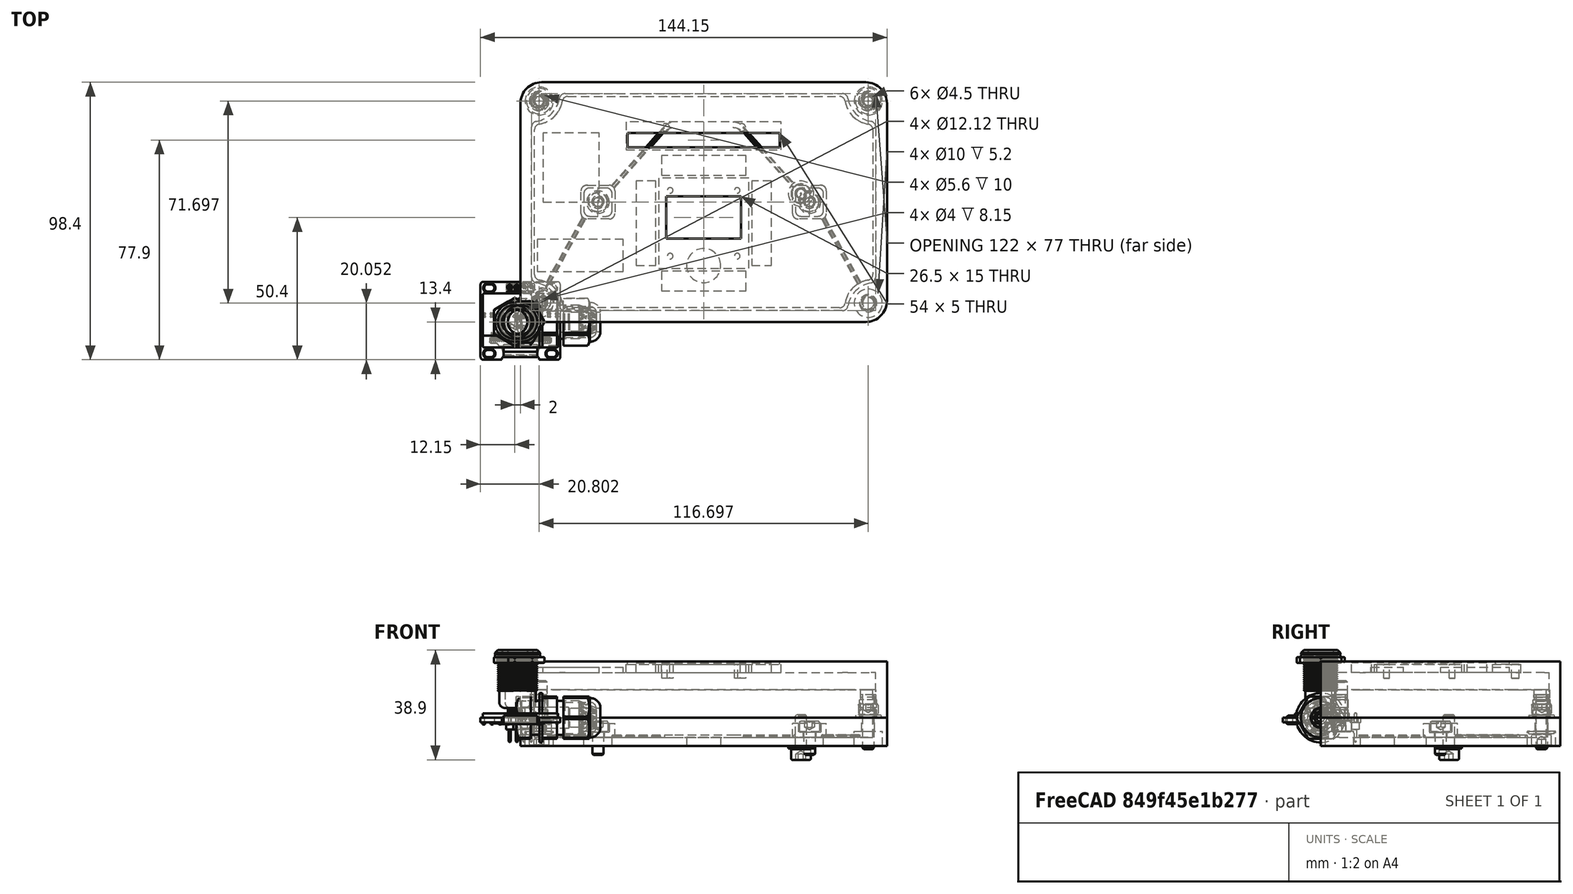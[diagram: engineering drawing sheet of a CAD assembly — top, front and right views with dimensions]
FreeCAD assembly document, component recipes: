
FREECAD ASSEMBLY — COMPONENT RECIPES ("FirstDraft_backup")

This assembly document has 6 components, labeled P0..P5 below (a component is one placed body or linked part). 2 of them carry a construction recipe — the FreeCAD feature program that regenerates the part from scratch, quoted from this document or its linked companion documents; the rest are supplied as boundary geometry only. No exploded tour is included for this assembly.
COMPONENT P0 — geometry summary ("Assembly"; no construction recipe available for this part):
  bounding box: 130.0 x 85.0 x 34.9 mm
  tessellated surface: 4,214 triangles
  volume: 3711431108486188694012094726733340963305844583327814948994821597056413378475866344786778061308690432 mm^3 (962395765290224016531339386291263704260556717746490642713404556607119533521990315734207654002688% of its bounding box)
COMPONENT P1 — recipe-attached ("Base", modeled in this document).
Construction recipe (the document's own serialized feature program — sketch geometry with constraints, then the solid features built on it; lengths are millimeters unless a unit is written):

FEATURE [PartDesign::ShapeBinder] ShapeBinder
  Support = -> [Pocket]
  TraceSupport = true
FEATURE [Sketcher::SketchObject] Sketch010
  ExternalGeometry = -> [ShapeBinder]
  FullyConstrained = true
  MapMode = 5
  Placement = pos=(0,0,0) rot=(1,0,0;3.14159rad)
  Support = -> [ShapeBinder]
  sketch-geometry (23):
    g0: GeomPoint X=5 Y=-5 Z=0
    g1: GeomPoint X=125 Y=-80 Z=0
    g2: GeomPoint X=65 Y=-42.5 Z=0
    g3: ArcOfCircle CenterX=5 CenterY=-80 CenterZ=0 NormalX=0 NormalY=0 NormalZ=1 AngleXU=0 Radius=10 StartAngle=0.167448 EndAngle=1.40335
    g4: ArcOfCircle CenterX=7 CenterY=-68.1678 CenterZ=0 NormalX=0 NormalY=0 NormalZ=1 AngleXU=0 Radius=2 StartAngle=3.14159 EndAngle=4.54494
    g5: ArcOfCircle CenterX=5 CenterY=-5 CenterZ=0 NormalX=0 NormalY=0 NormalZ=1 AngleXU=0 Radius=10 StartAngle=4.87984 EndAngle=6.11574
    g6: ArcOfCircle CenterX=125 CenterY=-5 CenterZ=0 NormalX=0 NormalY=0 NormalZ=1 AngleXU=0 Radius=10 StartAngle=3.30904 EndAngle=4.54494
    g7: ArcOfCircle CenterX=125 CenterY=-80 CenterZ=0 NormalX=0 NormalY=0 NormalZ=1 AngleXU=0 Radius=10 StartAngle=1.73824 EndAngle=2.97414
    g8: LineSegment StartX=5 StartY=-80 StartZ=0 EndX=125 EndY=-80 EndZ=0
    g9: LineSegment StartX=125 StartY=-80 StartZ=0 EndX=125 EndY=-5 EndZ=0
    g10: LineSegment StartX=5 StartY=-5 StartZ=0 EndX=5 EndY=-80 EndZ=0
    g11: ArcOfCircle CenterX=7 CenterY=-16.8322 CenterZ=0 NormalX=0 NormalY=0 NormalZ=1 AngleXU=0 Radius=2 StartAngle=1.73824 EndAngle=3.14159
    g12: ArcOfCircle CenterX=123 CenterY=-16.8322 CenterZ=0 NormalX=0 NormalY=0 NormalZ=1 AngleXU=0 Radius=2 StartAngle=9e-16 EndAngle=1.40335
    g13: ArcOfCircle CenterX=16.8322 CenterY=-7 CenterZ=0 NormalX=0 NormalY=0 NormalZ=1 AngleXU=0 Radius=2 StartAngle=1.5708 EndAngle=2.97414
    g14: ArcOfCircle CenterX=113.168 CenterY=-7 CenterZ=0 NormalX=0 NormalY=0 NormalZ=1 AngleXU=0 Radius=2 StartAngle=0.167448 EndAngle=1.5708
    g15: ArcOfCircle CenterX=123 CenterY=-68.1678 CenterZ=0 NormalX=0 NormalY=0 NormalZ=1 AngleXU=0 Radius=2 StartAngle=4.87984 EndAngle=6.28319
    g16: ArcOfCircle CenterX=113.168 CenterY=-78 CenterZ=0 NormalX=0 NormalY=0 NormalZ=1 AngleXU=0 Radius=2 StartAngle=4.71239 EndAngle=6.11574
    g17: ArcOfCircle CenterX=16.8322 CenterY=-78 CenterZ=0 NormalX=0 NormalY=0 NormalZ=1 AngleXU=0 Radius=2 StartAngle=3.30904 EndAngle=4.71239
    g18: LineSegment StartX=5 StartY=-5 StartZ=0 EndX=125 EndY=-5 EndZ=0
    g19: LineSegment StartX=5 StartY=-16.8322 StartZ=0 EndX=5 EndY=-68.1678 EndZ=0
    g20: LineSegment StartX=125 StartY=-68.1678 StartZ=0 EndX=125 EndY=-16.8322 EndZ=0
    g21: LineSegment StartX=113.168 StartY=-5 StartZ=0 EndX=16.8322 EndY=-5 EndZ=0
    g22: LineSegment StartX=16.8322 StartY=-80 StartZ=0 EndX=113.168 EndY=-80 EndZ=0
  constraints (54):
    c: Tangent(g3,g4) = 1.5708
    c: Coincident(g7,g1)
    c: Coincident(g8,g9)
    c: Coincident(g10,g8)
    c: Horizontal(g8)
    c: Vertical(g9)
    c: Vertical(g10)
    c: Coincident(g8,g3)
    c: Coincident(g9,g6)
    c: Coincident(g0,g5)
    c: Symmetric(g3,g6,g2)
    c: Tangent(g5,g11) = 1.5708
    c: Tangent(g6,g12) = 1.5708
    c: Tangent(g5,g13) = 1.5708
    c: Tangent(g6,g14) = 1.5708
    c: Tangent(g7,g15) = 1.5708
    c: Tangent(g7,g16) = 1.5708
    c: Equal(g3,g5)
    c: Equal(g5,g6)
    c: Equal(g6,g7)
    c: Radius(g3) = 10
    c: Equal(g4,g13)
    c: Equal(g13,g11)
    c: Equal(g11,g14)
    c: Equal(g12,g15)
    c: Tangent(g16,g8) = -1.5708
    c: Tangent(g4,g10) = -1.5708
    c: Coincident(g8,g7)
    c: Tangent(g17,g8) = -1.5708
    c: Tangent(g17,g3) = 1.5708
    c: Radius(g17) = 2
    c: Tangent(g12,g9) = -1.5708
    c: Tangent(g15,g9) = -1.5708
    c: Tangent(g11,g10) = -1.5708
    c: Coincident(g18,g5)
    c: Horizontal(g18)
    c: Coincident(g18,g6)
    c: Coincident(g10,g5)
    c: Tangent(g13,g18) = 1.5708
    c: Tangent(g14,g18) = 1.5708
    c: Equal(g11,g12)
    c: Equal(g14,g17)
    c: Equal(g17,g16)
    c: Symmetric(g-3,g-5,g2)
    c: Coincident(g19,g11)
    c: Coincident(g19,g4)
    c: Coincident(g20,g15)
    c: Coincident(g20,g12)
    c: Coincident(g21,g14)
    c: Coincident(g21,g13)
    c: DistanceY(g5,g-4) = 1
    c: DistanceX(g-5,g11) = 1
    c: Coincident(g22,g17)
    c: Coincident(g22,g16)
FEATURE [Sketcher::SketchObject] Sketch011
  ExternalGeometry = -> [ShapeBinder]
  FullyConstrained = true
  MapMode = 5
  Placement = pos=(0,0,0) rot=(1,0,0;3.14159rad)
  Support = -> [ShapeBinder]
  sketch-geometry (12):
    g0: LineSegment StartX=7.5 StartY=0 StartZ=0 EndX=122.5 EndY=0 EndZ=0
    g1: LineSegment StartX=130 StartY=-7.5 StartZ=0 EndX=130 EndY=-77.5 EndZ=0
    g2: LineSegment StartX=122.5 StartY=-85 StartZ=0 EndX=7.5 EndY=-85 EndZ=0
    g3: LineSegment StartX=0 StartY=-77.5 StartZ=0 EndX=0 EndY=-7.5 EndZ=0
    g4: ArcOfCircle CenterX=7.5 CenterY=-7.5 CenterZ=0 NormalX=0 NormalY=0 NormalZ=1 AngleXU=0 Radius=7.5 StartAngle=1.5708 EndAngle=3.14159
    g5: GeomPoint X=0 Y=0 Z=0
    g6: ArcOfCircle CenterX=122.5 CenterY=-7.5 CenterZ=0 NormalX=0 NormalY=0 NormalZ=1 AngleXU=0 Radius=7.5 StartAngle=0 EndAngle=1.5708
    g7: GeomPoint X=130 Y=0 Z=0
    g8: ArcOfCircle CenterX=122.5 CenterY=-77.5 CenterZ=0 NormalX=0 NormalY=0 NormalZ=1 AngleXU=0 Radius=7.5 StartAngle=4.71239 EndAngle=6.28319
    g9: GeomPoint X=130 Y=-85 Z=0
    g10: ArcOfCircle CenterX=7.5 CenterY=-77.5 CenterZ=0 NormalX=0 NormalY=0 NormalZ=1 AngleXU=0 Radius=7.5 StartAngle=3.14159 EndAngle=4.71239
    g11: GeomPoint X=0 Y=-85 Z=0
  constraints (23):
    c: Horizontal(g0)
    c: Vertical(g1)
    c: Vertical(g3)
    c: Coincident(g5,g-1)
    c: PointOnObject(g5,g3)
    c: Tangent(g0,g4) = 1.5708
    c: Tangent(g3,g4) = 1.5708
    c: PointOnObject(g7,g1)
    c: PointOnObject(g7,g0)
    c: Tangent(g1,g6) = 1.5708
    c: Tangent(g0,g6) = 1.5708
    c: PointOnObject(g9,g1)
    c: PointOnObject(g9,g2)
    c: Tangent(g1,g8) = 1.5708
    c: Tangent(g2,g8) = 1.5708
    c: PointOnObject(g11,g2)
    c: PointOnObject(g11,g3)
    c: Tangent(g2,g10) = 1.5708
    c: Tangent(g3,g10) = 1.5708
    c: Coincident(g2,g-4)
    c: Coincident(g2,g-4)
    c: Coincident(g-3,g1)
    c: Coincident(g0,g-5)
FEATURE [PartDesign::Pad] Pad003
  Direction = (0,0,-1)
  Length = 10
  Length2 = 10
  Profile = -> Sketch011
  ReferenceAxis = -> Sketch011 [N_Axis]
  Type = 0
FEATURE [PartDesign::Pocket] Pocket005
  BaseFeature = -> Pad003
  Direction = (0,0,1)
  Length = 7
  Length2 = 5
  Profile = -> Sketch010
  ReferenceAxis = -> Sketch010 [N_Axis]
  Reversed = true
  Type = 0
FEATURE [Sketcher::SketchObject] Sketch012
  ExternalGeometry = -> [ShapeBinder]
  FullyConstrained = true
  MapMode = 5
  Placement = pos=(0,0,-10) rot=(1,0,0;3.14159rad)
  Support = -> [Pocket005]
  sketch-geometry (4):
    g0: Circle CenterX=6.65146 CenterY=-6.65148 CenterZ=0 NormalX=0 NormalY=0 NormalZ=1 AngleXU=0 Radius=2.8
    g1: Circle CenterX=123.349 CenterY=-6.65148 CenterZ=0 NormalX=0 NormalY=0 NormalZ=1 AngleXU=0 Radius=2.8
    g2: Circle CenterX=123.349 CenterY=-78.3485 CenterZ=0 NormalX=0 NormalY=0 NormalZ=1 AngleXU=0 Radius=2.8
    g3: Circle CenterX=6.65146 CenterY=-78.3485 CenterZ=0 NormalX=0 NormalY=0 NormalZ=1 AngleXU=0 Radius=2.8
  constraints (8):
    c: Coincident(g1,g-4)
    c: Coincident(g2,g-5)
    c: Coincident(g3,g-6)
    c: Coincident(g0,g-3)
    c: Equal(g0,g-3)
    c: Equal(g0,g1)
    c: Equal(g1,g2)
    c: Equal(g2,g3)
FEATURE [PartDesign::Hole] Hole
  BaseFeature = -> Pocket005
  CustomThreadClearance = 0
  Depth = 314.401
  DepthType = 1
  Diameter = 4.5
  DrillForDepth = false
  DrillPoint = 1
  DrillPointAngle = 118
  HoleCutCountersinkAngle = 90
  HoleCutCustomValues = false
  HoleCutDepth = 5.2
  HoleCutDiameter = 10
  HoleCutType = 12
  ModelThread = false
  Profile = -> Sketch012
  Tapered = false
  TaperedAngle = 90
  ThreadClass = 0
  ThreadDepth = 314.401
  ThreadDepthType = 0
  ThreadDirection = 0
  ThreadFit = 0
  ThreadSize = 11
  ThreadType = 1
  Threaded = false
  UseCustomThreadClearance = false
FEATURE [Sketcher::SketchObject] Sketch013
  ExternalGeometry = -> [ShapeBinder]
  FullyConstrained = true
  MapMode = 5
  Placement = pos=(0,0,0) rot=(1,0,0;3.14159rad)
  Support = -> [ShapeBinder]
  sketch-geometry (46):
    g0: GeomPoint X=5 Y=-5 Z=0
    g1: GeomPoint X=125 Y=-80 Z=0
    g2: GeomPoint X=65 Y=-42.5 Z=0
    g3: ArcOfCircle CenterX=5 CenterY=-80 CenterZ=0 NormalX=0 NormalY=0 NormalZ=1 AngleXU=0 Radius=10 StartAngle=0.167448 EndAngle=1.40335
    g4: ArcOfCircle CenterX=7 CenterY=-68.1678 CenterZ=0 NormalX=0 NormalY=0 NormalZ=1 AngleXU=0 Radius=2 StartAngle=3.14159 EndAngle=4.54494
    g5: ArcOfCircle CenterX=5 CenterY=-5 CenterZ=0 NormalX=0 NormalY=0 NormalZ=1 AngleXU=0 Radius=10 StartAngle=4.87984 EndAngle=6.11574
    g6: ArcOfCircle CenterX=125 CenterY=-5 CenterZ=0 NormalX=0 NormalY=0 NormalZ=1 AngleXU=0 Radius=10 StartAngle=3.30904 EndAngle=4.54494
    g7: ArcOfCircle CenterX=125 CenterY=-80 CenterZ=0 NormalX=0 NormalY=0 NormalZ=1 AngleXU=0 Radius=10 StartAngle=1.73824 EndAngle=2.97414
    g8: LineSegment StartX=5 StartY=-80 StartZ=0 EndX=125 EndY=-80 EndZ=0
    g9: LineSegment StartX=125 StartY=-80 StartZ=0 EndX=125 EndY=-5 EndZ=0
    g10: LineSegment StartX=5 StartY=-5 StartZ=0 EndX=5 EndY=-80 EndZ=0
    g11: ArcOfCircle CenterX=7 CenterY=-16.8322 CenterZ=0 NormalX=0 NormalY=0 NormalZ=1 AngleXU=0 Radius=2 StartAngle=1.73824 EndAngle=3.14159
    g12: ArcOfCircle CenterX=123 CenterY=-16.8322 CenterZ=0 NormalX=0 NormalY=0 NormalZ=1 AngleXU=0 Radius=2 StartAngle=-9e-16 EndAngle=1.40335
    g13: ArcOfCircle CenterX=16.8322 CenterY=-7 CenterZ=0 NormalX=0 NormalY=0 NormalZ=1 AngleXU=0 Radius=2 StartAngle=1.5708 EndAngle=2.97414
    g14: ArcOfCircle CenterX=113.168 CenterY=-7 CenterZ=0 NormalX=0 NormalY=0 NormalZ=1 AngleXU=0 Radius=2 StartAngle=0.167448 EndAngle=1.5708
    g15: ArcOfCircle CenterX=123 CenterY=-68.1678 CenterZ=0 NormalX=0 NormalY=0 NormalZ=1 AngleXU=0 Radius=2 StartAngle=4.87984 EndAngle=6.28319
    g16: ArcOfCircle CenterX=113.168 CenterY=-78 CenterZ=0 NormalX=0 NormalY=0 NormalZ=1 AngleXU=0 Radius=2 StartAngle=4.71239 EndAngle=6.11574
    g17: ArcOfCircle CenterX=16.8322 CenterY=-78 CenterZ=0 NormalX=0 NormalY=0 NormalZ=1 AngleXU=0 Radius=2 StartAngle=3.30904 EndAngle=4.71239
    g18: LineSegment StartX=5 StartY=-5 StartZ=0 EndX=125 EndY=-5 EndZ=0
    g19: LineSegment StartX=5 StartY=-16.8322 StartZ=0 EndX=5 EndY=-68.1678 EndZ=0
    g20: LineSegment StartX=125 StartY=-68.1678 StartZ=0 EndX=125 EndY=-16.8322 EndZ=0
    g21: LineSegment StartX=113.168 StartY=-5 StartZ=0 EndX=16.8322 EndY=-5 EndZ=0
    g22: LineSegment StartX=16.8322 StartY=-80 StartZ=0 EndX=113.168 EndY=-80 EndZ=0
    g23: GeomPoint X=4 Y=-4 Z=0
    g24: GeomPoint X=126 Y=-81 Z=0
    g25: GeomPoint X=65 Y=-42.5 Z=0
    g26: ArcOfCircle CenterX=4 CenterY=-81 CenterZ=0 NormalX=0 NormalY=0 NormalZ=1 AngleXU=0 Radius=10 StartAngle=0.167448 EndAngle=1.40335
    g27: ArcOfCircle CenterX=6 CenterY=-69.1678 CenterZ=0 NormalX=0 NormalY=0 NormalZ=1 AngleXU=0 Radius=2 StartAngle=3.14159 EndAngle=4.54494
    g28: ArcOfCircle CenterX=4 CenterY=-4 CenterZ=0 NormalX=0 NormalY=0 NormalZ=1 AngleXU=0 Radius=10 StartAngle=4.87984 EndAngle=6.11574
    g29: ArcOfCircle CenterX=126 CenterY=-4 CenterZ=0 NormalX=0 NormalY=0 NormalZ=1 AngleXU=0 Radius=10 StartAngle=3.30904 EndAngle=4.54494
    g30: ArcOfCircle CenterX=126 CenterY=-81 CenterZ=0 NormalX=0 NormalY=0 NormalZ=1 AngleXU=0 Radius=10 StartAngle=1.73824 EndAngle=2.97414
    g31: LineSegment StartX=4 StartY=-81 StartZ=0 EndX=126 EndY=-81 EndZ=0
    g32: LineSegment StartX=126 StartY=-81 StartZ=0 EndX=126 EndY=-4 EndZ=0
    g33: LineSegment StartX=4 StartY=-4 StartZ=0 EndX=4 EndY=-81 EndZ=0
    g34: ArcOfCircle CenterX=6 CenterY=-15.8322 CenterZ=0 NormalX=0 NormalY=0 NormalZ=1 AngleXU=0 Radius=2 StartAngle=1.73824 EndAngle=3.14159
    g35: ArcOfCircle CenterX=124 CenterY=-15.8322 CenterZ=0 NormalX=0 NormalY=0 NormalZ=1 AngleXU=0 Radius=2 StartAngle=3e-16 EndAngle=1.40335
    g36: ArcOfCircle CenterX=15.8322 CenterY=-6 CenterZ=0 NormalX=0 NormalY=0 NormalZ=1 AngleXU=0 Radius=2 StartAngle=1.5708 EndAngle=2.97414
    g37: ArcOfCircle CenterX=114.168 CenterY=-6 CenterZ=0 NormalX=0 NormalY=0 NormalZ=1 AngleXU=0 Radius=2 StartAngle=0.167448 EndAngle=1.5708
    g38: ArcOfCircle CenterX=124 CenterY=-69.1678 CenterZ=0 NormalX=0 NormalY=0 NormalZ=1 AngleXU=0 Radius=2 StartAngle=4.87984 EndAngle=6.28319
    g39: ArcOfCircle CenterX=114.168 CenterY=-79 CenterZ=0 NormalX=0 NormalY=0 NormalZ=1 AngleXU=0 Radius=2 StartAngle=4.71239 EndAngle=6.11574
    g40: ArcOfCircle CenterX=15.8322 CenterY=-79 CenterZ=0 NormalX=0 NormalY=0 NormalZ=1 AngleXU=0 Radius=2 StartAngle=3.30904 EndAngle=4.71239
    g41: LineSegment StartX=4 StartY=-4 StartZ=0 EndX=126 EndY=-4 EndZ=0
    g42: LineSegment StartX=4 StartY=-15.8322 StartZ=0 EndX=4 EndY=-69.1678 EndZ=0
    g43: LineSegment StartX=126 StartY=-69.1678 StartZ=0 EndX=126 EndY=-15.8322 EndZ=0
    g44: LineSegment StartX=114.168 StartY=-4 StartZ=0 EndX=15.8322 EndY=-4 EndZ=0
    g45: LineSegment StartX=15.8322 StartY=-81 StartZ=0 EndX=114.168 EndY=-81 EndZ=0
  constraints (107):
    c: Tangent(g3,g4) = 1.5708
    c: Coincident(g7,g1)
    c: Coincident(g8,g9)
    c: Coincident(g10,g8)
    c: Horizontal(g8)
    c: Vertical(g9)
    c: Vertical(g10)
    c: Coincident(g8,g3)
    c: Coincident(g9,g6)
    c: Coincident(g0,g5)
    c: Symmetric(g3,g6,g2)
    c: Tangent(g5,g11) = 1.5708
    c: Tangent(g6,g12) = 1.5708
    c: Tangent(g5,g13) = 1.5708
    c: Tangent(g6,g14) = 1.5708
    c: Tangent(g7,g15) = 1.5708
    c: Tangent(g7,g16) = 1.5708
    c: Equal(g3,g5)
    c: Equal(g5,g6)
    c: Equal(g6,g7)
    c: Radius(g3) = 10
    c: Equal(g4,g13)
    c: Equal(g13,g11)
    c: Equal(g11,g14)
    c: Equal(g12,g15)
    c: Tangent(g16,g8) = -1.5708
    c: Tangent(g4,g10) = -1.5708
    c: Coincident(g8,g7)
    c: Tangent(g17,g8) = -1.5708
    c: Tangent(g17,g3) = 1.5708
    c: Radius(g17) = 2
    c: Tangent(g12,g9) = -1.5708
    c: Tangent(g15,g9) = -1.5708
    c: Tangent(g11,g10) = -1.5708
    c: Coincident(g18,g5)
    c: Horizontal(g18)
    c: Coincident(g18,g6)
    c: Coincident(g10,g5)
    c: Tangent(g13,g18) = 1.5708
    c: Tangent(g14,g18) = 1.5708
    c: Equal(g11,g12)
    c: Equal(g14,g17)
    c: Equal(g17,g16)
    c: Coincident(g19,g11)
    c: Coincident(g19,g4)
    c: Coincident(g20,g15)
    c: Coincident(g20,g12)
    c: Coincident(g21,g14)
    c: Coincident(g21,g13)
    c: Coincident(g22,g17)
    c: Coincident(g22,g16)
    c: Tangent(g26,g27) = 1.5708
    c: Coincident(g30,g24)
    c: Coincident(g31,g32)
    c: Coincident(g33,g31)
    c: Horizontal(g31)
    c: Vertical(g32)
    c: Vertical(g33)
    c: Coincident(g31,g26)
    c: Coincident(g32,g29)
    c: Coincident(g23,g28)
    c: Symmetric(g26,g29,g25)
    c: Tangent(g28,g34) = 1.5708
    c: Tangent(g29,g35) = 1.5708
    c: Tangent(g28,g36) = 1.5708
    c: Tangent(g29,g37) = 1.5708
    c: Tangent(g30,g38) = 1.5708
    c: Tangent(g30,g39) = 1.5708
    c: Equal(g26,g28)
    c: Equal(g28,g29)
    c: Equal(g29,g30)
    c: Radius(g26) = 10
    c: Equal(g27,g36)
    c: Equal(g36,g34)
    c: Equal(g34,g37)
    c: Equal(g35,g38)
    c: Tangent(g39,g31) = -1.5708
    c: Tangent(g27,g33) = -1.5708
    c: Coincident(g31,g30)
    c: Tangent(g40,g31) = -1.5708
    c: Tangent(g40,g26) = 1.5708
    c: Radius(g40) = 2
    c: Tangent(g35,g32) = -1.5708
    c: Tangent(g38,g32) = -1.5708
    c: Tangent(g34,g33) = -1.5708
    c: Coincident(g41,g28)
    c: Horizontal(g41)
    c: Coincident(g41,g29)
    c: Coincident(g33,g28)
    c: Tangent(g36,g41) = 1.5708
    c: Tangent(g37,g41) = 1.5708
    c: Equal(g34,g35)
    c: Equal(g37,g40)
    c: Equal(g40,g39)
    c: Coincident(g42,g34)
    c: Coincident(g42,g27)
    c: Coincident(g43,g38)
    c: Coincident(g43,g35)
    c: Coincident(g44,g37)
    c: Coincident(g44,g36)
    c: Coincident(g45,g40)
    c: Coincident(g45,g39)
    c: Symmetric(g28,g30,g2)
    c: Coincident(g34,g-3)
    c: Coincident(g38,g-4)
    c: DistanceX(g27,g4) = 1
    c: DistanceY(g40,g17) = 1
FEATURE [PartDesign::Pad] Pad004
  BaseFeature = -> Hole
  Direction = (0,0,-1)
  Length = 10
  Length2 = 10
  Profile = -> Sketch013
  ReferenceAxis = -> Sketch013 [N_Axis]
  Reversed = true
  Type = 0
FEATURE [PartDesign::CoordinateSystem] LCS_1
  AttacherType = Attacher::AttachEngine3D
  MapMode = 5
  Support = -> [Pad004]
FEATURE [PartDesign::Line] HoleAxis_1
  AttacherType = Attacher::AttachEngineLine
  Length = 4.79083
  MapMode = 19
  Placement = pos=(123.349,6.65148,-4.8) rot=(0,1,0;3.14159rad)
  ResizeMode = 1
  Support = -> [Pad004]
FEATURE [PartDesign::Line] HoleAxis_2
  AttacherType = Attacher::AttachEngineLine
  Length = 4.79083
  MapMode = 19
  Placement = pos=(123.349,78.3485,-4.8) rot=(0,1,0;3.14159rad)
  ResizeMode = 1
  Support = -> [Pad004]
FEATURE [PartDesign::Line] HoleAxis_3
  AttacherType = Attacher::AttachEngineLine
  Length = 4.79083
  MapMode = 19
  Placement = pos=(6.65146,78.3485,-4.8) rot=(0,1,0;3.14159rad)
  ResizeMode = 1
  Support = -> [Pad004]
FEATURE [PartDesign::Line] HoleAxis_4
  AttacherType = Attacher::AttachEngineLine
  Length = 4.79083
  MapMode = 19
  Placement = pos=(6.65146,6.65148,-4.8) rot=(0,1,0;3.14159rad)
  ResizeMode = 1
  Support = -> [Pad004]
FEATURE [Sketcher::SketchObject] Sketch014
  ExternalGeometry = -> [Pad004]
  FullyConstrained = true
  MapMode = 5
  Placement = pos=(0,0,-7) rot=(0,0,1;0rad)
  Support = -> [Pad004]
  sketch-geometry (3):
    g0: Circle CenterX=65 CenterY=20 CenterZ=0 NormalX=0 NormalY=0 NormalZ=1 AngleXU=0 Radius=6
    g1: GeomPoint X=65 Y=0 Z=0
    g2: LineSegment StartX=65 StartY=0 StartZ=0 EndX=65 EndY=20 EndZ=0
  constraints (6):
    c: Diameter(g0) = 12
    c: Symmetric(g-3,g-3,g1)
    c: Coincident(g2,g1)
    c: Coincident(g2,g0)
    c: Vertical(g2)
    c: DistanceY(g2,g2) = 20
FEATURE [PartDesign::Hole] Hole001
  BaseFeature = -> Pad004
  CustomThreadClearance = 0
  Depth = 25
  DepthType = 0
  Diameter = 12.1
  DrillForDepth = false
  DrillPoint = 1
  DrillPointAngle = 118
  HoleCutCountersinkAngle = 90
  HoleCutCustomValues = false
  HoleCutDepth = 0
  HoleCutDiameter = 13.6
  HoleCutType = 0
  ModelThread = false
  Profile = -> Sketch014
  Refine = true
  Tapered = false
  TaperedAngle = 90
  ThreadClass = 0
  ThreadDepth = 25
  ThreadDepthType = 0
  ThreadDirection = 0
  ThreadFit = 0
  ThreadSize = 19
  ThreadType = 1
  Threaded = false
  UseCustomThreadClearance = false
FEATURE [Sketcher::SketchObject] Sketch015
  ExternalGeometry = -> [HoleAxis_2,HoleAxis_4]
  FullyConstrained = true
  MapMode = 5
  Placement = pos=(0,0,-7) rot=(0,0,1;0rad)
  Support = -> [Hole001]
  sketch-geometry (24):
    g0: ArcOfCircle CenterX=23.5 CenterY=46.5 CenterZ=0 NormalX=0 NormalY=0 NormalZ=1 AngleXU=0 Radius=2 StartAngle=1.5708 EndAngle=3.14159
    g1: LineSegment StartX=23.5 StartY=48.5 StartZ=0 EndX=31.5 EndY=48.5 EndZ=0
    g2: ArcOfCircle CenterX=31.5 CenterY=46.5 CenterZ=0 NormalX=0 NormalY=0 NormalZ=1 AngleXU=0 Radius=2 StartAngle=0 EndAngle=1.5708
    g3: LineSegment StartX=33.5 StartY=46.5 StartZ=0 EndX=33.5 EndY=38.5 EndZ=0
    g4: ArcOfCircle CenterX=31.5 CenterY=38.5 CenterZ=0 NormalX=0 NormalY=0 NormalZ=1 AngleXU=0 Radius=2 StartAngle=4.71239 EndAngle=6.28319
    g5: LineSegment StartX=31.5 StartY=36.5 StartZ=0 EndX=23.5 EndY=36.5 EndZ=0
    g6: ArcOfCircle CenterX=23.5 CenterY=38.5 CenterZ=0 NormalX=0 NormalY=0 NormalZ=1 AngleXU=0 Radius=2 StartAngle=3.14159 EndAngle=4.71239
    g7: LineSegment StartX=21.5 StartY=38.5 StartZ=0 EndX=21.5 EndY=46.5 EndZ=0
    g8: GeomPoint X=21.5 Y=48.5 Z=0
    g9: GeomPoint X=33.5 Y=36.5 Z=0
    g10: ArcOfCircle CenterX=98.5 CenterY=46.5 CenterZ=0 NormalX=0 NormalY=0 NormalZ=1 AngleXU=0 Radius=2 StartAngle=1.5708 EndAngle=3.14159
    g11: LineSegment StartX=98.5 StartY=48.5 StartZ=0 EndX=106.5 EndY=48.5 EndZ=0
    g12: ArcOfCircle CenterX=106.5 CenterY=46.5 CenterZ=0 NormalX=0 NormalY=0 NormalZ=1 AngleXU=0 Radius=2 StartAngle=6e-16 EndAngle=1.5708
    g13: LineSegment StartX=108.5 StartY=46.5 StartZ=0 EndX=108.5 EndY=38.5 EndZ=0
    g14: ArcOfCircle CenterX=106.5 CenterY=38.5 CenterZ=0 NormalX=0 NormalY=0 NormalZ=1 AngleXU=0 Radius=2 StartAngle=4.71239 EndAngle=6.28319
    g15: LineSegment StartX=106.5 StartY=36.5 StartZ=0 EndX=98.5 EndY=36.5 EndZ=0
    g16: ArcOfCircle CenterX=98.5 CenterY=38.5 CenterZ=0 NormalX=0 NormalY=0 NormalZ=1 AngleXU=0 Radius=2 StartAngle=3.14159 EndAngle=4.71239
    g17: LineSegment StartX=96.5 StartY=38.5 StartZ=0 EndX=96.5 EndY=46.5 EndZ=0
    g18: GeomPoint X=96.5 Y=48.5 Z=0
    g19: GeomPoint X=108.5 Y=36.5 Z=0
    g20: GeomPoint X=27.5 Y=42.5 Z=0
    g21: GeomPoint X=102.5 Y=42.5 Z=0
    g22: GeomPoint X=65 Y=42.5 Z=0
    g23: LineSegment StartX=27.5 StartY=42.5 StartZ=0 EndX=102.5 EndY=42.5 EndZ=0
  constraints (53):
    c: Tangent(g0,g1) = 1.5708
    c: Tangent(g1,g2) = 1.5708
    c: Tangent(g2,g3) = 1.5708
    c: Tangent(g3,g4) = 1.5708
    c: Tangent(g4,g5) = 1.5708
    c: Tangent(g5,g6) = 1.5708
    c: Tangent(g6,g7) = 1.5708
    c: Tangent(g7,g0) = 1.5708
    c: Horizontal(g1)
    c: Horizontal(g5)
    c: Vertical(g3)
    c: Vertical(g7)
    c: Equal(g2,g4)
    c: Equal(g4,g6)
    c: PointOnObject(g8,g1)
    c: PointOnObject(g8,g7)
    c: PointOnObject(g9,g3)
    c: PointOnObject(g9,g5)
    c: Tangent(g10,g11) = 1.5708
    c: Tangent(g11,g12) = 1.5708
    c: Tangent(g12,g13) = 1.5708
    c: Tangent(g13,g14) = 1.5708
    c: Tangent(g14,g15) = 1.5708
    c: Tangent(g15,g16) = 1.5708
    c: Tangent(g16,g17) = 1.5708
    c: Tangent(g17,g10) = 1.5708
    c: Horizontal(g11)
    c: Horizontal(g15)
    c: Vertical(g13)
    c: Vertical(g17)
    c: Equal(g10,g12)
    c: Equal(g12,g14)
    c: Equal(g14,g16)
    c: PointOnObject(g18,g11)
    c: PointOnObject(g18,g17)
    c: PointOnObject(g19,g13)
    c: PointOnObject(g19,g15)
    c: Symmetric(g16,g12,g21)
    c: Symmetric(g2,g6,g20)
    c: Equal(g1,g11)
    c: Equal(g3,g13)
    c: Symmetric(g-4,g-3,g22)
    c: Symmetric(g21,g20,g22)
    c: Coincident(g23,g20)
    c: Coincident(g23,g21)
    c: Horizontal(g23)
    c: Equal(g2,g0)
    c: Equal(g6,g16)
    c: Radius(g4) = 2
    c: DistanceX(g8,g9) = 12  'Breite Klickfixadapter'
    c: DistanceY(g9,g8) = 12
    c: DistanceX(g23,g23) = 75
    c: DistanceX(g8,g19) = 87
FEATURE [PartDesign::Pad] Pad005
  BaseFeature = -> Hole001
  Direction = (0,0,1)
  Length = 5
  Length2 = 10
  Profile = -> Sketch015
  ReferenceAxis = -> Sketch015 [N_Axis]
  Refine = true
  Type = 0
FEATURE [Sketcher::SketchObject] Sketch017
  ExternalGeometry = -> [Pad005]
  FullyConstrained = true
  MapMode = 5
  Placement = pos=(0,0,-10) rot=(1,0,0;3.14159rad)
  Support = -> [Pad005]
  sketch-geometry (22):
    g0: ArcOfCircle CenterX=24.5 CenterY=-39.5 CenterZ=0 NormalX=0 NormalY=0 NormalZ=1 AngleXU=0 Radius=2 StartAngle=1.5708 EndAngle=3.14159
    g1: LineSegment StartX=24.5 StartY=-37.5 StartZ=0 EndX=30.5 EndY=-37.5 EndZ=0
    g2: ArcOfCircle CenterX=30.5 CenterY=-39.5 CenterZ=0 NormalX=0 NormalY=0 NormalZ=1 AngleXU=0 Radius=2 StartAngle=-2.7e-15 EndAngle=1.5708
    g3: LineSegment StartX=32.5 StartY=-39.5 StartZ=0 EndX=32.5 EndY=-45.5 EndZ=0
    g4: ArcOfCircle CenterX=30.5 CenterY=-45.5 CenterZ=0 NormalX=0 NormalY=0 NormalZ=1 AngleXU=0 Radius=2 StartAngle=4.71239 EndAngle=6.28319
    g5: LineSegment StartX=30.5 StartY=-47.5 StartZ=0 EndX=24.5 EndY=-47.5 EndZ=0
    g6: ArcOfCircle CenterX=24.5 CenterY=-45.5 CenterZ=0 NormalX=0 NormalY=0 NormalZ=1 AngleXU=0 Radius=2 StartAngle=3.14159 EndAngle=4.71239
    g7: LineSegment StartX=22.5 StartY=-45.5 StartZ=0 EndX=22.5 EndY=-39.5 EndZ=0
    g8: GeomPoint X=22.5 Y=-37.5 Z=0
    g9: GeomPoint X=32.5 Y=-47.5 Z=0
    g10: ArcOfCircle CenterX=99.5 CenterY=-39.5 CenterZ=0 NormalX=0 NormalY=0 NormalZ=1 AngleXU=0 Radius=2 StartAngle=1.5708 EndAngle=3.14159
    g11: LineSegment StartX=99.5 StartY=-37.5 StartZ=0 EndX=105.5 EndY=-37.5 EndZ=0
    g12: ArcOfCircle CenterX=105.5 CenterY=-39.5 CenterZ=0 NormalX=0 NormalY=0 NormalZ=1 AngleXU=0 Radius=2 StartAngle=-7.1e-15 EndAngle=1.5708
    g13: LineSegment StartX=107.5 StartY=-39.5 StartZ=0 EndX=107.5 EndY=-45.5 EndZ=0
    g14: ArcOfCircle CenterX=105.5 CenterY=-45.5 CenterZ=0 NormalX=0 NormalY=0 NormalZ=1 AngleXU=0 Radius=2 StartAngle=4.71239 EndAngle=6.28319
    g15: LineSegment StartX=105.5 StartY=-47.5 StartZ=0 EndX=99.5 EndY=-47.5 EndZ=0
    g16: ArcOfCircle CenterX=99.5 CenterY=-45.5 CenterZ=0 NormalX=0 NormalY=0 NormalZ=1 AngleXU=0 Radius=2 StartAngle=3.14159 EndAngle=4.71239
    g17: LineSegment StartX=97.5 StartY=-45.5 StartZ=0 EndX=97.5 EndY=-39.5 EndZ=0
    g18: GeomPoint X=97.5 Y=-37.5 Z=0
    g19: GeomPoint X=107.5 Y=-47.5 Z=0
    g20: GeomPoint X=27.5 Y=-42.5 Z=0
    g21: GeomPoint X=102.5 Y=-42.5 Z=0
  constraints (49):
    c: Equal(g4,g6)
    c: PointOnObject(g8,g1)
    c: PointOnObject(g8,g7)
    c: PointOnObject(g9,g3)
    c: PointOnObject(g9,g5)
    c: Tangent(g10,g11) = 1.5708
    c: Tangent(g11,g12) = 1.5708
    c: Tangent(g12,g13) = 1.5708
    c: Tangent(g13,g14) = 1.5708
    c: Tangent(g14,g15) = 1.5708
    c: Tangent(g15,g16) = 1.5708
    c: Tangent(g16,g17) = 1.5708
    c: Tangent(g17,g10) = 1.5708
    c: Horizontal(g11)
    c: Horizontal(g15)
    c: Vertical(g13)
    c: Vertical(g17)
    c: Equal(g10,g12)
    c: Equal(g12,g14)
    c: Equal(g14,g16)
    c: PointOnObject(g18,g11)
    c: PointOnObject(g18,g17)
    c: PointOnObject(g19,g13)
    c: PointOnObject(g19,g15)
    c: Equal(g10,g4)
    c: Horizontal(g1)
    c: Vertical(g3)
    c: Vertical(g7)
    c: Horizontal(g5)
    c: Tangent(g6,g7) = 1.5708
    c: Tangent(g3,g4) = 1.5708
    c: Tangent(g1,g2) = 1.5708
    c: Tangent(g0,g7) = 1.5708
    c: Tangent(g0,g1) = 1.5708
    c: Tangent(g3,g2) = 1.5708
    c: Tangent(g5,g4) = 1.5708
    c: Tangent(g5,g6) = 1.5708
    c: Equal(g6,g0)
    c: Equal(g0,g2)
    c: Radius(g0) = 2
    c: DistanceX(g0,g2) = 10
    c: DistanceY(g4,g1) = 10
    c: Symmetric(g6,g2,g20)
    c: Symmetric(g-4,g-3,g20)
    c: Equal(g3,g13)
    c: Symmetric(g16,g12,g21)
    c: Symmetric(g-5,g-6,g21)
    c: Equal(g13,g11)
    c: DistanceX(g6,g13) = 85
FEATURE [PartDesign::Pocket] Pocket007
  BaseFeature = -> Pad005
  Direction = (0,0,1)
  Length = 3
  Length2 = 5
  Profile = -> Sketch017
  ReferenceAxis = -> Sketch017 [N_Axis]
  Refine = true
  Type = 0
FEATURE [Sketcher::SketchObject] Sketch016
  ExternalGeometry = -> [Pad005]
  FullyConstrained = true
  MapMode = 5
  Placement = pos=(0,0,-2) rot=(0,0,1;0rad)
  Support = -> [Pocket007]
  sketch-geometry (2):
    g0: Circle CenterX=27.5 CenterY=42.5 CenterZ=0 NormalX=0 NormalY=0 NormalZ=1 AngleXU=0 Radius=2
    g1: Circle CenterX=102.5 CenterY=42.5 CenterZ=0 NormalX=0 NormalY=0 NormalZ=1 AngleXU=0 Radius=2
  constraints (4):
    c: Equal(g0,g1)
    c: Symmetric(g-5,g-6,g0)
    c: Symmetric(g-4,g-3,g1)
    c: Diameter(g0) = 4
FEATURE [PartDesign::Hole] Hole002
  BaseFeature = -> Pocket007
  CustomThreadClearance = 0
  Depth = 8
  DepthType = 0
  Diameter = 4.5
  DrillForDepth = false
  DrillPoint = 1
  DrillPointAngle = 118
  HoleCutCountersinkAngle = 90
  HoleCutCustomValues = false
  HoleCutDepth = 3.2
  HoleCutDiameter = 8
  HoleCutType = 6
  ModelThread = false
  Profile = -> Sketch016
  Refine = true
  Tapered = false
  TaperedAngle = 90
  ThreadClass = 0
  ThreadDepth = 8
  ThreadDepthType = 0
  ThreadDirection = 0
  ThreadFit = 0
  ThreadSize = 11
  ThreadType = 1
  Threaded = false
  UseCustomThreadClearance = false
FEATURE [Sketcher::SketchObject] Sketch020  label="Stabilisierung - Pfad"
  ExternalGeometry = -> [Hole002]
  FullyConstrained = true
  MapMode = 5
  Placement = pos=(0,0,-7) rot=(0,0,1;0rad)
  Support = -> [Hole002]
  sketch-geometry (13):
    g0: LineSegment StartX=14.6316 StartY=70.3684 StartZ=0 EndX=10.7634 EndY=74.2366 EndZ=0
    g1: LineSegment StartX=15.0973 StartY=69.6369 StartZ=0 EndX=22.9672 EndY=47.9672 EndZ=0
    g2: LineSegment StartX=12.0711 StartY=72.9289 StartZ=0 EndX=14.8601 EndY=78.3333 EndZ=0
    g3: LineSegment StartX=12.0711 StartY=72.9289 StartZ=0 EndX=6.66667 EndY=70.1399 EndZ=0
    g4: ArcOfCircle CenterX=13.2174 CenterY=68.9542 CenterZ=0 NormalX=0 NormalY=0 NormalZ=1 AngleXU=0 Radius=2 StartAngle=0.348363 EndAngle=0.785398
    g5: GeomPoint X=14.9457 Y=70.0543 Z=0
    g6: LineSegment StartX=10.7634 StartY=74.2366 StartZ=0 EndX=22.9672 EndY=47.9672 EndZ=0
    g7: LineSegment StartX=21.5 StartY=46.5 StartZ=0 EndX=23.5 EndY=48.5 EndZ=0
    g8: LineSegment StartX=6.66667 StartY=70.1399 StartZ=0 EndX=14.8601 EndY=78.3333 EndZ=0
    g9: LineSegment StartX=22.7885 StartY=37.2115 StartZ=0 EndX=9.10088 EndY=12.4259 EndZ=0
    g10: LineSegment StartX=6.66667 StartY=14.8601 StartZ=0 EndX=14.8601 EndY=6.66667 EndZ=0
    g11: LineSegment StartX=22.7885 StartY=37.2115 StartZ=0 EndX=22.9672 EndY=47.9672 EndZ=0
    g12: LineSegment StartX=21.5 StartY=38.5 StartZ=0 EndX=23.5 EndY=36.5 EndZ=0
  constraints (32):
    c: Perpendicular(g-4,g1)
    c: Coincident(g2,g-3)
    c: Coincident(g3,g-3)
    c: Equal(g3,g2)
    c: PointOnObject(g5,g0)
    c: PointOnObject(g5,g1)
    c: Tangent(g0,g4) = -1.5708
    c: Tangent(g1,g4) = 1.5708
    c: Radius(g4) = 2
    c: PointOnObject(g4,g6)
    c: Coincident(g6,g1)
    c: Coincident(g8,g3)
    c: Coincident(g8,g2)
    c: Coincident(g6,g0)
    c: PointOnObject(g0,g8)
    c: Coincident(g2,g3)
    c: PointOnObject(g2,g0)
    c: PointOnObject(g2,g-3)
    c: Perpendicular(g0,g-3,g2) = 4.71239
    c: PointOnObject(g1,g7)
    c: Coincident(g7,g-4)
    c: Coincident(g7,g-4)
    c: Coincident(g10,g-5)
    c: Coincident(g10,g-5)
    c: PointOnObject(g9,g10)
    c: Perpendicular(g-5,g9)
    c: Coincident(g11,g9)
    c: Coincident(g11,g1)
    c: Perpendicular(g-6,g9)
    c: Coincident(g12,g-6)
    c: Coincident(g12,g-6)
    c: PointOnObject(g9,g12)
FEATURE [Sketcher::SketchObject] Sketch019  label="Stabilisierung - Profil"
  FullyConstrained = true
  MapMode = 7
  Placement = pos=(15.0973,69.6369,-7) rot=(-0.123474,0.701696,0.701696;3.3873rad)
  Support = -> [Sketch020]
  sketch-geometry (7):
    g0: LineSegment StartX=-1 StartY=0 StartZ=0 EndX=1 EndY=0 EndZ=0
    g1: ArcOfCircle CenterX=0 CenterY=0.522986 CenterZ=0 NormalX=0 NormalY=0 NormalZ=1 AngleXU=0 Radius=0.477014 StartAngle=0.261799 EndAngle=2.87979
    g2: ArcOfCircle CenterX=1 CenterY=0.477014 CenterZ=0 NormalX=0 NormalY=0 NormalZ=1 AngleXU=0 Radius=0.477014 StartAngle=3.40339 EndAngle=4.71239
    g3: LineSegment StartX=0.53924 StartY=0.353553 StartZ=0 EndX=0.46076 EndY=0.646447 EndZ=0
    g4: LineSegment StartX=-0.53924 StartY=0.353553 StartZ=0 EndX=-0.46076 EndY=0.646447 EndZ=0
    g5: ArcOfCircle CenterX=-1 CenterY=0.477014 CenterZ=0 NormalX=0 NormalY=0 NormalZ=1 AngleXU=0 Radius=0.477014 StartAngle=4.71239 EndAngle=6.02139
    g6: GeomPoint X=0 Y=1 Z=0
  constraints (16):
    c: PointOnObject(g0,g-1)
    c: Symmetric(g0,g0,g-1)
    c: PointOnObject(g1,g-2)
    c: Tangent(g3,g1) = -1.5708
    c: Tangent(g3,g2) = 1.5708
    c: Tangent(g2,g0) = -1.5708
    c: Tangent(g4,g5) = -1.5708
    c: Tangent(g1,g4) = 1.5708
    c: Equal(g4,g3)
    c: PointOnObject(g6,g-2)
    c: PointOnObject(g6,g1)
    c: DistanceY(g-1,g6) = 1
    c: DistanceX(g0,g0) = 2
    c: Tangent(g0,g5) = -1.5708
    c: Angle(g-2,g3) = 0.261799
    c: Equal(g1,g5)
FEATURE [PartDesign::AdditivePipe] AdditivePipe
  AuxilleryCurvelinear = true
  AuxillerySpineTangent = false
  BaseFeature = -> Hole002
  Binormal = (0,0,0)
  Mode = 0
  Profile = -> Sketch019
  Refine = true
  Spine = -> Sketch020
  SpineTangent = false
  Transformation = 0
  Transition = 0
FEATURE [PartDesign::Line] DatumLine
  AttacherType = Attacher::AttachEngineLine
  Length = 20
  MapMode = 43
  Placement = pos=(65,0,0) rot=(0,0.707107,0.707107;3.14159rad)
  ResizeMode = 0
  Support = -> [Pad003]
FEATURE [PartDesign::Plane] DatumPlane
  Length = 64.8324
  MapMode = 4
  Placement = pos=(65,0,0) rot=(0,-1,0;1.5708rad)
  ResizeMode = 0
  Support = -> [DatumLine]
  Width = 124.832
FEATURE [PartDesign::Mirrored] Mirrored
  BaseFeature = -> AdditivePipe
  MirrorPlane = -> DatumPlane
  Originals = -> [AdditivePipe]
  Overlap = 1
  Refine = true
FEATURE [Sketcher::SketchObject] Sketch021
  ExternalGeometry = -> [Mirrored,DatumPlane]
  FullyConstrained = true
  MapMode = 5
  Placement = pos=(0,0,-7) rot=(0,0,1;0rad)
  Support = -> [Mirrored]
  sketch-geometry (21):
    g0: LineSegment StartX=31.5 StartY=46.5 StartZ=0 EndX=51.0091 EndY=68.3317 EndZ=0
    g1: LineSegment StartX=54.7374 StartY=70 StartZ=0 EndX=75.2626 EndY=70 EndZ=0
    g2: LineSegment StartX=78.9909 StartY=68.3317 StartZ=0 EndX=98.5 EndY=46.5 EndZ=0
    g3: LineSegment StartX=98.5 StartY=46.5 StartZ=0 EndX=98.5 EndY=38.5 EndZ=0
    g4: LineSegment StartX=98.5 StartY=38.5 StartZ=0 EndX=77.5 EndY=20 EndZ=0
    g5: LineSegment StartX=77.5 StartY=20 StartZ=0 EndX=52.5 EndY=20 EndZ=0
    g6: LineSegment StartX=52.5 StartY=20 StartZ=0 EndX=31.5 EndY=38.5 EndZ=0
    g7: LineSegment StartX=31.5 StartY=38.5 StartZ=0 EndX=31.5 EndY=46.5 EndZ=0
    g8-g12: Circle x5 (B-spline internal-alignment scaffolding for g13; pole/knot coordinates omitted)
    g13: BSplineCurve PolesCount=5 KnotsCount=3 Degree=3 IsPeriodic=0
    g14: GeomPoint X=31.5 Y=38.5 Z=0
    g15: GeomPoint X=65 Y=32.5 Z=0
    g16: GeomPoint X=98.5 Y=38.5 Z=0
    g17: ArcOfCircle CenterX=54.7374 CenterY=65 CenterZ=0 NormalX=0 NormalY=0 NormalZ=1 AngleXU=0 Radius=5 StartAngle=1.5708 EndAngle=2.41232
    g18: GeomPoint X=52.5 Y=70 Z=0
    g19: ArcOfCircle CenterX=75.2626 CenterY=65 CenterZ=0 NormalX=0 NormalY=0 NormalZ=1 AngleXU=0 Radius=5 StartAngle=0.729277 EndAngle=1.5708
    g20: GeomPoint X=77.5 Y=70 Z=0
  constraints (41):
    c: Coincident(g6,g5)
    c: Coincident(g7,g0)
    c: Coincident(g2,g-5)
    c: Coincident(g3,g2)
    c: Coincident(g3,g4)
    c: Coincident(g6,g7)
    c: Coincident(g6,g-4)
    c: Coincident(g0,g-3)
    c: Coincident(g5,g4)
    c: Symmetric(g20,g18,g-6)
    c: Symmetric(g5,g4,g-6)
    c: Coincident(g13,g7)
    c: Weight(g8) = 1
    c: Equal(g8,g9)
    c: Coincident(g9,g5)
    c: Equal(g8,g10)
    c: Equal(g8,g11)
    c: Equal(g8,g12)
    c: Coincident(g13,g3)
    c: InternalAlignment(g8-g12 -> g13) x5
    c: InternalAlignment(g14,g13)
    c: InternalAlignment(g15,g13)
    c: InternalAlignment(g16,g13)
    c: PointOnObject(g10,g-6)
    c: PointOnObject(g-7,g5)
    c: DistanceX(g18,g20) = 25
    c: DistanceY(g-7,g10) = 25
    c: Coincident(g3,g-8)
    c: Coincident(g11,g4)
    c: DistanceY(g10,g20) = 25
    c: PointOnObject(g18,g0)
    c: PointOnObject(g18,g1)
    c: Tangent(g0,g17) = 1.5708
    c: Tangent(g1,g17) = 1.5708
    c: PointOnObject(g20,g1)
    c: PointOnObject(g20,g2)
    c: Tangent(g1,g19) = 1.5708
    c: Tangent(g2,g19) = 1.5708
    c: Equal(g19,g17)
    c: Radius(g17) = 5
    c: DistanceX(g5,g5) = 25
FEATURE [Sketcher::SketchObject] Sketch055  label="Stabilisierung - Profil002"
  FullyConstrained = true
  MapMode = 7
  Placement = pos=(78.9909,68.3317,-7) rot=(0.879973,0.335893,0.335893;1.69831rad)
  Support = -> [Sketch021]
  sketch-geometry (7):
    g0: LineSegment StartX=-1 StartY=0 StartZ=0 EndX=1 EndY=0 EndZ=0
    g1: ArcOfCircle CenterX=0 CenterY=0.522986 CenterZ=0 NormalX=0 NormalY=0 NormalZ=1 AngleXU=0 Radius=0.477014 StartAngle=0.261799 EndAngle=2.87979
    g2: ArcOfCircle CenterX=1 CenterY=0.477014 CenterZ=0 NormalX=0 NormalY=0 NormalZ=1 AngleXU=0 Radius=0.477014 StartAngle=3.40339 EndAngle=4.71239
    g3: LineSegment StartX=0.53924 StartY=0.353553 StartZ=0 EndX=0.46076 EndY=0.646447 EndZ=0
    g4: LineSegment StartX=-0.53924 StartY=0.353553 StartZ=0 EndX=-0.46076 EndY=0.646447 EndZ=0
    g5: ArcOfCircle CenterX=-1 CenterY=0.477014 CenterZ=0 NormalX=0 NormalY=0 NormalZ=1 AngleXU=0 Radius=0.477014 StartAngle=4.71239 EndAngle=6.02139
    g6: GeomPoint X=0 Y=1 Z=0
  constraints (16):
    c: PointOnObject(g0,g-1)
    c: Symmetric(g0,g0,g-1)
    c: PointOnObject(g1,g-2)
    c: Tangent(g3,g1) = -1.5708
    c: Tangent(g3,g2) = 1.5708
    c: Tangent(g2,g0) = -1.5708
    c: Tangent(g4,g5) = -1.5708
    c: Tangent(g1,g4) = 1.5708
    c: Equal(g4,g3)
    c: PointOnObject(g6,g-2)
    c: PointOnObject(g6,g1)
    c: DistanceY(g-1,g6) = 1
    c: DistanceX(g0,g0) = 2
    c: Tangent(g0,g5) = -1.5708
    c: Angle(g-2,g3) = 0.261799
    c: Equal(g1,g5)
FEATURE [PartDesign::AdditivePipe] AdditivePipe001
  AuxilleryCurvelinear = true
  AuxillerySpineTangent = false
  BaseFeature = -> Mirrored
  Binormal = (0,0,0)
  Mode = 1
  Profile = -> Sketch055
  Refine = true
  Spine = -> Sketch021
  SpineTangent = false
  Transformation = 0
  Transition = 0
FEATURE [PartDesign::Body] Body  label="Base"
  Group = -> [ShapeBinder,Sketch010,Sketch011,Pad003,Pocket005,Sketch012,Hole,Sketch013,Pad004,LCS_1,HoleAxis_1,HoleAxis_2,HoleAxis_3,HoleAxis_4,Sketch014,Hole001,Sketch015,Pad005,Sketch016,Sketch017,Pocket007,Hole002,Sketch019,Sketch020,AdditivePipe,DatumLine,DatumPlane,Mirrored,Sketch021,Sketch055,AdditivePipe001]
  Origin = -> Origin
  Tip = -> AdditivePipe001
COMPONENT P2 — geometry summary ("PG012"; no construction recipe available for this part):
  bounding box: 29.9 x 17.5 x 15.2 mm
  tessellated surface: 992 triangles
  volume: 3827 mm^3 (48% of its bounding box)
  symmetry: 2-fold rotationally symmetric about the z axis
COMPONENT P3 — geometry summary ("Double-Switch"; no construction recipe available for this part):
  bounding box: 32.9 x 23.8 x 17.0 mm
  tessellated surface: 5,444 triangles
  volume: 4589 mm^3 (34% of its bounding box)
COMPONENT P4 — recipe-attached ("Front inkl. Fasteners", modeled in this document).
Construction recipe (the document's own serialized feature program — sketch geometry with constraints, then the solid features built on it; lengths are millimeters unless a unit is written):

FEATURE [PartDesign::AdditiveBox] Box002
  AttacherType = Attacher::AttachEngine3D
  Height = 20
  Length = 130
  Width = 85
FEATURE [Sketcher::SketchObject] Sketch001
  ExternalGeometry = -> [Box002]
  FullyConstrained = true
  MapMode = 5
  Placement = pos=(0,0,0) rot=(1,0,0;3.14159rad)
  Support = -> [Box002]
  sketch-geometry (23):
    g0: LineSegment StartX=15.8322 StartY=-4 StartZ=0 EndX=114.168 EndY=-4 EndZ=0
    g1: LineSegment StartX=126 StartY=-15.8322 StartZ=0 EndX=126 EndY=-69.1678 EndZ=0
    g2: LineSegment StartX=114.168 StartY=-81 StartZ=0 EndX=15.8322 EndY=-81 EndZ=0
    g3: LineSegment StartX=4 StartY=-69.1678 StartZ=0 EndX=4 EndY=-15.8322 EndZ=0
    g4: GeomPoint X=4 Y=-4 Z=0
    g5: GeomPoint X=126 Y=-81 Z=0
    g6: GeomPoint X=65 Y=-42.5 Z=0
    g7: ArcOfCircle CenterX=4 CenterY=-81 CenterZ=0 NormalX=0 NormalY=0 NormalZ=1 AngleXU=0 Radius=10 StartAngle=0.167448 EndAngle=1.40335
    g8: ArcOfCircle CenterX=6 CenterY=-69.1678 CenterZ=0 NormalX=0 NormalY=0 NormalZ=1 AngleXU=0 Radius=2 StartAngle=3.14159 EndAngle=4.54494
    g9: ArcOfCircle CenterX=15.8322 CenterY=-79 CenterZ=0 NormalX=0 NormalY=0 NormalZ=1 AngleXU=0 Radius=2 StartAngle=3.30904 EndAngle=4.71239
    g10: ArcOfCircle CenterX=4 CenterY=-4 CenterZ=0 NormalX=0 NormalY=0 NormalZ=1 AngleXU=0 Radius=10 StartAngle=4.87984 EndAngle=6.11574
    g11: ArcOfCircle CenterX=126 CenterY=-4 CenterZ=0 NormalX=0 NormalY=0 NormalZ=1 AngleXU=0 Radius=10 StartAngle=3.30904 EndAngle=4.54494
    g12: ArcOfCircle CenterX=126 CenterY=-81 CenterZ=0 NormalX=0 NormalY=0 NormalZ=1 AngleXU=0 Radius=10 StartAngle=1.73824 EndAngle=2.97414
    g13: LineSegment StartX=4 StartY=-81 StartZ=0 EndX=126 EndY=-81 EndZ=0
    g14: LineSegment StartX=126 StartY=-81 StartZ=0 EndX=126 EndY=-4 EndZ=0
    g15: LineSegment StartX=126 StartY=-4 StartZ=0 EndX=4 EndY=-4 EndZ=0
    g16: LineSegment StartX=4 StartY=-4 StartZ=0 EndX=4 EndY=-81 EndZ=0
    g17: ArcOfCircle CenterX=6 CenterY=-15.8322 CenterZ=0 NormalX=0 NormalY=0 NormalZ=1 AngleXU=0 Radius=2 StartAngle=1.73824 EndAngle=3.14159
    g18: ArcOfCircle CenterX=124 CenterY=-15.8322 CenterZ=0 NormalX=0 NormalY=0 NormalZ=1 AngleXU=0 Radius=2 StartAngle=0 EndAngle=1.40335
    g19: ArcOfCircle CenterX=15.8322 CenterY=-6 CenterZ=0 NormalX=0 NormalY=0 NormalZ=1 AngleXU=0 Radius=2 StartAngle=1.5708 EndAngle=2.97414
    g20: ArcOfCircle CenterX=114.168 CenterY=-6 CenterZ=0 NormalX=0 NormalY=0 NormalZ=1 AngleXU=0 Radius=2 StartAngle=0.167448 EndAngle=1.5708
    g21: ArcOfCircle CenterX=124 CenterY=-69.1678 CenterZ=0 NormalX=0 NormalY=0 NormalZ=1 AngleXU=0 Radius=2 StartAngle=4.87984 EndAngle=6.28319
    g22: ArcOfCircle CenterX=114.168 CenterY=-79 CenterZ=0 NormalX=0 NormalY=0 NormalZ=1 AngleXU=0 Radius=2 StartAngle=4.71239 EndAngle=6.11574
  constraints (56):
    c: Horizontal(g0)
    c: Horizontal(g2)
    c: Vertical(g1)
    c: Vertical(g3)
    c: PointOnObject(g4,g0)
    c: PointOnObject(g4,g3)
    c: PointOnObject(g5,g1)
    c: PointOnObject(g5,g2)
    c: Symmetric(g-6,g-4,g6)
    c: Tangent(g7,g8) = 1.5708
    c: Tangent(g3,g8) = 1.5708
    c: Tangent(g2,g9) = 1.5708
    c: Tangent(g7,g9) = 1.5708
    c: Coincident(g12,g5)
    c: Coincident(g13,g14)
    c: Coincident(g14,g15)
    c: Coincident(g15,g16)
    c: Coincident(g16,g13)
    c: Horizontal(g13)
    c: Horizontal(g15)
    c: Vertical(g14)
    c: Vertical(g16)
    c: Coincident(g13,g7)
    c: Coincident(g14,g11)
    c: Coincident(g4,g10)
    c: Symmetric(g7,g11,g6)
    c: Tangent(g3,g17) = 1.5708
    c: Tangent(g10,g17) = 1.5708
    c: Tangent(g1,g18) = 1.5708
    c: Tangent(g11,g18) = 1.5708
    c: Tangent(g10,g19) = 1.5708
    c: Tangent(g0,g19) = 1.5708
    c: Tangent(g11,g20) = 1.5708
    c: Tangent(g0,g20) = 1.5708
    c: Tangent(g1,g21) = 1.5708
    c: Tangent(g12,g21) = 1.5708
    c: Tangent(g2,g22) = 1.5708
    c: Tangent(g12,g22) = 1.5708
    c: PointOnObject(g0,g15)
    c: PointOnObject(g3,g16)
    c: PointOnObject(g1,g14)
    c: DistanceX(g-6,g7) = 4
    c: DistanceY(g-6,g7) = 4
    c: PointOnObject(g2,g13)
    c: Equal(g7,g10)
    c: Equal(g10,g11)
    c: Equal(g11,g12)
    c: Radius(g7) = 10
    c: Equal(g9,g8)
    c: Equal(g8,g19)
    c: Equal(g19,g17)
    c: Equal(g17,g20)
    c: Equal(g20,g18)
    c: Equal(g18,g21)
    c: Equal(g21,g22)
    c: Radius(g9) = 2
FEATURE [PartDesign::Pocket] Pocket001
  BaseFeature = -> Box002
  Direction = (0,0,1)
  Length = 16
  Length2 = 100
  Profile = -> Sketch001
  ReferenceAxis = -> Sketch001 [N_Axis]
  Type = 0
  expr: Length = <<Box002>>.Height - 4mm
FEATURE [Sketcher::SketchObject] Sketch002
  ExternalGeometry = -> [Pocket001]
  FullyConstrained = true
  MapMode = 5
  Placement = pos=(0,0,16) rot=(1,0,0;3.14159rad)
  Support = -> [Pocket001]
  sketch-geometry (11):
    g0: LineSegment StartX=49 StartY=-19 StartZ=0 EndX=81 EndY=-19 EndZ=0
    g1: LineSegment StartX=81 StartY=-19 StartZ=0 EndX=81 EndY=-51 EndZ=0
    g2: LineSegment StartX=81 StartY=-51 StartZ=0 EndX=49 EndY=-51 EndZ=0
    g3: LineSegment StartX=49 StartY=-51 StartZ=0 EndX=49 EndY=-19 EndZ=0
    g4: GeomPoint X=65 Y=-4 Z=0
    g5: LineSegment StartX=65 StartY=-4 StartZ=0 EndX=65 EndY=-19 EndZ=0
    g6: LineSegment StartX=37.5 StartY=-61 StartZ=0 EndX=92.5 EndY=-61 EndZ=0
    g7: LineSegment StartX=92.5 StartY=-61 StartZ=0 EndX=92.5 EndY=-71 EndZ=0
    g8: LineSegment StartX=92.5 StartY=-71 StartZ=0 EndX=37.5 EndY=-71 EndZ=0
    g9: LineSegment StartX=37.5 StartY=-71 StartZ=0 EndX=37.5 EndY=-61 EndZ=0
    g10: LineSegment StartX=65 StartY=-19 StartZ=0 EndX=65 EndY=-61 EndZ=0
  constraints (29):
    c: Coincident(g0,g1)
    c: Coincident(g1,g2)
    c: Coincident(g2,g3)
    c: Coincident(g3,g0)
    c: Horizontal(g0)
    c: Horizontal(g2)
    c: Vertical(g1)
    c: Vertical(g3)
    c: Coincident(g5,g4)
    c: Vertical(g5)
    c: Symmetric(g0,g0,g5)
    c: DistanceY(g5,g5) = 15
    c: DistanceY(g1,g1) = 32
    c: Equal(g1,g0)
    c: Coincident(g6,g7)
    c: Coincident(g7,g8)
    c: Coincident(g8,g9)
    c: Coincident(g9,g6)
    c: Horizontal(g6)
    c: Horizontal(g8)
    c: Vertical(g7)
    c: Vertical(g9)
    c: DistanceX(g6,g6) = 55
    c: DistanceY(g7,g7) = 10
    c: Coincident(g10,g5)
    c: Vertical(g10)
    c: Symmetric(g6,g6,g10)
    c: DistanceY(g6,g1) = 10
    c: Symmetric(g-3,g-3,g4)
FEATURE [PartDesign::Pocket] Pocket002  label="Platz OLED und LED-Strip"
  BaseFeature = -> Pocket001
  Direction = (0,0,1)
  Length = 3
  Length2 = 100
  Profile = -> Sketch002
  Type = 0
FEATURE [Sketcher::SketchObject] Sketch003
  ExternalGeometry = -> [Sketch002,Pocket002]
  FullyConstrained = true
  MapMode = 5
  Placement = pos=(0,0,16) rot=(1,0,0;3.14159rad)
  Support = -> [Pocket002]
  sketch-geometry (10):
    g0: LineSegment StartX=51.75 StartY=-29.5 StartZ=0 EndX=78.25 EndY=-29.5 EndZ=0
    g1: LineSegment StartX=78.25 StartY=-29.5 StartZ=0 EndX=78.25 EndY=-44.5 EndZ=0
    g2: LineSegment StartX=78.25 StartY=-44.5 StartZ=0 EndX=51.75 EndY=-44.5 EndZ=0
    g3: LineSegment StartX=51.75 StartY=-44.5 StartZ=0 EndX=51.75 EndY=-29.5 EndZ=0
    g4: LineSegment StartX=38 StartY=-62 StartZ=0 EndX=92 EndY=-62 EndZ=0
    g5: LineSegment StartX=92 StartY=-62 StartZ=0 EndX=92 EndY=-67 EndZ=0
    g6: LineSegment StartX=92 StartY=-67 StartZ=0 EndX=38 EndY=-67 EndZ=0
    g7: LineSegment StartX=38 StartY=-67 StartZ=0 EndX=38 EndY=-62 EndZ=0
    g8: LineSegment StartX=65 StartY=-62 StartZ=0 EndX=65 EndY=-61 EndZ=0
    g9: LineSegment StartX=65 StartY=-29.5 StartZ=0 EndX=65 EndY=-19 EndZ=0
  constraints (28):
    c: Coincident(g0,g1)
    c: Coincident(g1,g2)
    c: Coincident(g2,g3)
    c: Coincident(g3,g0)
    c: Horizontal(g0)
    c: Horizontal(g2)
    c: Vertical(g1)
    c: Vertical(g3)
    c: DistanceX(g0,g0) = 26.5
    c: DistanceY(g1,g1) = 15
    c: Coincident(g4,g5)
    c: Coincident(g5,g6)
    c: Coincident(g6,g7)
    c: Coincident(g7,g4)
    c: Horizontal(g4)
    c: Horizontal(g6)
    c: Vertical(g5)
    c: Vertical(g7)
    c: DistanceX(g4,g-3) = 0.5
    c: Vertical(g8)
    c: Symmetric(g4,g4,g8)
    c: Symmetric(g-3,g-4,g8)
    c: DistanceY(g5,g5) = 5
    c: DistanceY(g4,g-3) = 1
    c: Vertical(g9)
    c: Symmetric(g0,g0,g9)
    c: DistanceY(g9,g9) = 10.5
    c: Symmetric(g-5,g-5,g9)
FEATURE [PartDesign::Pocket] Pocket003  label="Sichtausschnitt"
  BaseFeature = -> Pocket002
  Direction = (0,0,1)
  Length = 1.01
  Length2 = 100
  Profile = -> Sketch003
  ReferenceAxis = -> Sketch003 [N_Axis]
  Type = 1
FEATURE [Sketcher::SketchObject] Sketch004  label="Sketch Halter OLED"
  ExternalGeometry = -> [Sketch002]
  FullyConstrained = true
  MapMode = 5
  Placement = pos=(0,0,19) rot=(1,0,0;3.14159rad)
  Support = -> [Pocket003]
  sketch-geometry (9):
    g0: Circle CenterX=53.1 CenterY=-23.35 CenterZ=0 NormalX=0 NormalY=0 NormalZ=1 AngleXU=0 Radius=1
    g1: Circle CenterX=76.9 CenterY=-23.35 CenterZ=0 NormalX=0 NormalY=0 NormalZ=1 AngleXU=0 Radius=1
    g2: Circle CenterX=76.9 CenterY=-46.65 CenterZ=0 NormalX=0 NormalY=0 NormalZ=1 AngleXU=0 Radius=1
    g3: Circle CenterX=53.1 CenterY=-46.65 CenterZ=0 NormalX=0 NormalY=0 NormalZ=1 AngleXU=0 Radius=1
    g4: LineSegment StartX=53.1 StartY=-23.35 StartZ=0 EndX=76.9 EndY=-23.35 EndZ=0
    g5: LineSegment StartX=76.9 StartY=-23.35 StartZ=0 EndX=76.9 EndY=-46.65 EndZ=0
    g6: LineSegment StartX=76.9 StartY=-46.65 StartZ=0 EndX=53.1 EndY=-46.65 EndZ=0
    g7: LineSegment StartX=53.1 StartY=-46.65 StartZ=0 EndX=53.1 EndY=-23.35 EndZ=0
    g8: GeomPoint X=65 Y=-35 Z=0
  constraints (20):
    c: Coincident(g4,g5)
    c: Coincident(g5,g6)
    c: Coincident(g6,g7)
    c: Coincident(g7,g4)
    c: Horizontal(g4)
    c: Horizontal(g6)
    c: Vertical(g5)
    c: Vertical(g7)
    c: Coincident(g4,g0)
    c: Coincident(g5,g2)
    c: Coincident(g1,g4)
    c: Coincident(g3,g6)
    c: Equal(g0,g1)
    c: Equal(g1,g2)
    c: Equal(g2,g3)
    c: Diameter(g1) = 2
    c: DistanceX(g4,g4) = 23.8
    c: DistanceY(g5,g5) = 23.3
    c: Symmetric(g-4,g-6,g8)
    c: Symmetric(g3,g1,g8)
FEATURE [PartDesign::Pad] Pad  label="Halter OLED"
  BaseFeature = -> Pocket003
  Direction = (0,0,-1)
  Length = 5
  Length2 = 100
  Profile = -> Sketch004
  ReferenceAxis = -> Sketch004 [N_Axis]
  Type = 0
FEATURE [Sketcher::SketchObject] Sketch005
  ExternalGeometry = -> [Sketch002]
  FullyConstrained = true
  MapMode = 5
  Placement = pos=(0,0,16) rot=(1,0,0;3.14159rad)
  Support = -> [Pad]
  sketch-geometry (26):
    g0: LineSegment StartX=50 StartY=-11 StartZ=0 EndX=80 EndY=-11 EndZ=0
    g1: LineSegment StartX=80 StartY=-11 StartZ=0 EndX=80 EndY=-18 EndZ=0
    g2: LineSegment StartX=80 StartY=-18 StartZ=0 EndX=50 EndY=-18 EndZ=0
    g3: LineSegment StartX=50 StartY=-18 StartZ=0 EndX=50 EndY=-11 EndZ=0
    g4: LineSegment StartX=82 StartY=-20 StartZ=0 EndX=89 EndY=-20 EndZ=0
    g5: LineSegment StartX=89 StartY=-20 StartZ=0 EndX=89 EndY=-50 EndZ=0
    g6: LineSegment StartX=89 StartY=-50 StartZ=0 EndX=82 EndY=-50 EndZ=0
    g7: LineSegment StartX=82 StartY=-50 StartZ=0 EndX=82 EndY=-20 EndZ=0
    g8: LineSegment StartX=41 StartY=-20 StartZ=0 EndX=48 EndY=-20 EndZ=0
    g9: LineSegment StartX=48 StartY=-20 StartZ=0 EndX=48 EndY=-50 EndZ=0
    g10: LineSegment StartX=48 StartY=-50 StartZ=0 EndX=41 EndY=-50 EndZ=0
    g11: LineSegment StartX=41 StartY=-50 StartZ=0 EndX=41 EndY=-20 EndZ=0
    g12: LineSegment StartX=50 StartY=-52 StartZ=0 EndX=80 EndY=-52 EndZ=0
    g13: LineSegment StartX=80 StartY=-52 StartZ=0 EndX=80 EndY=-59 EndZ=0
    g14: LineSegment StartX=80 StartY=-59 StartZ=0 EndX=50 EndY=-59 EndZ=0
    g15: LineSegment StartX=50 StartY=-59 StartZ=0 EndX=50 EndY=-52 EndZ=0
    g16: LineSegment StartX=48 StartY=-18 StartZ=0 EndX=82 EndY=-18 EndZ=0
    g17: LineSegment StartX=82 StartY=-18 StartZ=0 EndX=82 EndY=-52 EndZ=0
    g18: LineSegment StartX=82 StartY=-52 StartZ=0 EndX=48 EndY=-52 EndZ=0
    g19: LineSegment StartX=48 StartY=-52 StartZ=0 EndX=48 EndY=-18 EndZ=0
    g20: GeomPoint X=65 Y=-35 Z=0
    g21: GeomPoint X=48 Y=-35 Z=0
    g22: GeomPoint X=116 Y=-18 Z=0
    g23: GeomPoint X=82 Y=-35 Z=0
    g24: GeomPoint X=65 Y=-52 Z=0
    g25: GeomPoint X=65 Y=-18 Z=0
  constraints (61):
    c: Coincident(g0,g1)
    c: Coincident(g1,g2)
    c: Coincident(g2,g3)
    c: Coincident(g3,g0)
    c: Horizontal(g0)
    c: Horizontal(g2)
    c: Vertical(g1)
    c: Vertical(g3)
    c: Coincident(g4,g5)
    c: Coincident(g5,g6)
    c: Coincident(g6,g7)
    c: Coincident(g7,g4)
    c: Horizontal(g4)
    c: Horizontal(g6)
    c: Vertical(g5)
    c: Vertical(g7)
    c: Coincident(g8,g9)
    c: Coincident(g9,g10)
    c: Coincident(g10,g11)
    c: Coincident(g11,g8)
    c: Horizontal(g8)
    c: Horizontal(g10)
    c: Vertical(g9)
    c: Vertical(g11)
    c: Coincident(g12,g13)
    c: Coincident(g13,g14)
    c: Coincident(g14,g15)
    c: Coincident(g15,g12)
    c: Horizontal(g12)
    c: Horizontal(g14)
    c: Vertical(g13)
    c: Vertical(g15)
    c: Equal(g4,g1)
    c: Equal(g1,g8)
    c: Equal(g8,g13)
    c: Coincident(g16,g17)
    c: Coincident(g17,g18)
    c: Coincident(g18,g19)
    c: Coincident(g19,g16)
    c: DistanceX(g-4,g16) = 1
    c: DistanceY(g-4,g16) = 1
    c: Symmetric(g16,g18,g20)
    c: Symmetric(g-6,g-4,g20)
    c: DistanceY(g15,g15) = 7
    c: Vertical(g19)
    c: Horizontal(g16)
    c: PointOnObject(g12,g18)
    c: Vertical(g17)
    c: Equal(g0,g11)
    c: Equal(g11,g5)
    c: Equal(g5,g14)
    c: DistanceY(g11,g11) = 30
    c: Symmetric(g18,g17,g24)
    c: Symmetric(g6,g4,g23)
    c: Symmetric(g16,g22,g16)
    c: Symmetric(g16,g18,g21)
    c: Symmetric(g8,g9,g21)
    c: Symmetric(g17,g16,g23)
    c: Symmetric(g12,g12,g24)
    c: Symmetric(g2,g1,g25)
    c: Symmetric(g16,g16,g25)
FEATURE [PartDesign::Pocket] Pocket004  label="Ausschnitte  Touch"
  BaseFeature = -> Pad
  Direction = (0,0,1)
  Length = 3.5
  Length2 = 100
  Profile = -> Sketch005
  Type = 0
FEATURE [Sketcher::SketchObject] Sketch007
  ExternalGeometry = -> [Pocket004,Sketch003]
  FullyConstrained = true
  MapMode = 5
  Placement = pos=(0,0,19) rot=(1,0,0;3.14159rad)
  Support = -> [Pocket004]
  sketch-geometry (5):
    g0: Circle CenterX=51.5 CenterY=-69 CenterZ=0 NormalX=0 NormalY=0 NormalZ=1 AngleXU=0 Radius=1.35
    g1: Circle CenterX=78.5 CenterY=-69 CenterZ=0 NormalX=0 NormalY=0 NormalZ=1 AngleXU=0 Radius=1.35
    g2: LineSegment StartX=51.5 StartY=-69 StartZ=0 EndX=78.5 EndY=-69 EndZ=0
    g3: LineSegment StartX=65 StartY=-71 StartZ=0 EndX=65 EndY=-67 EndZ=0
    g4: GeomPoint X=65 Y=-69 Z=0
  constraints (11):
    c: Coincident(g2,g0)
    c: Coincident(g2,g1)
    c: Horizontal(g2)
    c: Equal(g1,g0)
    c: Diameter(g0) = 2.7
    c: DistanceX(g2,g2) = 27
    c: Vertical(g3)
    c: Symmetric(g0,g1,g4)
    c: Symmetric(g3,g3,g4)
    c: Symmetric(g-5,g-5,g3)
    c: PointOnObject(g3,g-6)
FEATURE [PartDesign::Pad] Pad001  label="Halter LED Strip"
  BaseFeature = -> Pocket004
  Direction = (0,0,-1)
  Length = 5
  Length2 = 10
  Profile = -> Sketch007
  ReferenceAxis = -> Sketch007 [N_Axis]
  Type = 0
FEATURE [PartDesign::Fillet] Fillet
  Base = -> Pad001 [Edge3,Edge19,Edge1,Edge6]
  BaseFeature = -> Pad001
  Radius = 7.5
  SupportTransform = false
FEATURE [Sketcher::SketchObject] Sketch
  ExternalGeometry = -> [Fillet]
  FullyConstrained = true
  MapMode = 5
  Placement = pos=(0,0,0) rot=(1,0,0;3.14159rad)
  Support = -> [Fillet]
  sketch-geometry (17):
    g0: LineSegment StartX=6.65146 StartY=-6.65148 StartZ=0 EndX=123.349 EndY=-6.65148 EndZ=0
    g1: LineSegment StartX=123.349 StartY=-6.65148 StartZ=0 EndX=123.349 EndY=-78.3485 EndZ=0
    g2: LineSegment StartX=123.349 StartY=-78.3485 StartZ=0 EndX=6.65146 EndY=-78.3485 EndZ=0
    g3: LineSegment StartX=6.65146 StartY=-78.3485 StartZ=0 EndX=6.65146 EndY=-6.65148 EndZ=0
    g4: GeomPoint X=65 Y=-42.5 Z=0
    g5: Circle CenterX=123.349 CenterY=-6.65148 CenterZ=0 NormalX=0 NormalY=0 NormalZ=1 AngleXU=0 Radius=2.8
    g6: Circle CenterX=123.349 CenterY=-78.3485 CenterZ=0 NormalX=0 NormalY=0 NormalZ=1 AngleXU=0 Radius=2.8
    g7: Circle CenterX=6.65146 CenterY=-78.3485 CenterZ=0 NormalX=0 NormalY=0 NormalZ=1 AngleXU=0 Radius=2.8
    g8: Circle CenterX=6.65146 CenterY=-6.65148 CenterZ=0 NormalX=0 NormalY=0 NormalZ=1 AngleXU=0 Radius=2.8
    g9: LineSegment StartX=3.85146 StartY=-5.49168 StartZ=0 EndX=3.85146 EndY=-6.65148 EndZ=0
    g10: LineSegment StartX=3.85146 StartY=-5.49168 StartZ=0 EndX=9.34315 EndY=0 EndZ=0
    g11: LineSegment StartX=0 StartY=-4.3934 StartZ=0 EndX=4.3934 EndY=0 EndZ=0
    g12: LineSegment StartX=4.67157 StartY=-4.67157 StartZ=0 EndX=2.1967 EndY=-2.1967 EndZ=0
    g13: GeomPoint X=4.67157 Y=-4.67157 Z=0
    g14: GeomPoint X=2.1967 Y=-2.1967 Z=0
    g15: LineSegment StartX=11.0711 StartY=-11.0711 StartZ=0 EndX=22.1421 EndY=0 EndZ=0
    g16: LineSegment StartX=8.63137 StartY=-8.63137 StartZ=0 EndX=17.2627 EndY=0 EndZ=0
  constraints (45):
    c: Coincident(g0,g1)
    c: Coincident(g1,g2)
    c: Coincident(g2,g3)
    c: Coincident(g3,g0)
    c: Horizontal(g0)
    c: Horizontal(g2)
    c: Vertical(g1)
    c: Vertical(g3)
    c: Symmetric(g-3,g-4,g4)
    c: Symmetric(g2,g0,g4)
    c: Coincident(g5,g0)
    c: Coincident(g6,g1)
    c: Coincident(g7,g2)
    c: Diameter(g7) = 5.6
    c: Coincident(g8,g0)
    c: Equal(g5,g6)
    c: Equal(g6,g7)
    c: Equal(g7,g8)
    c: Vertical(g9)
    c: DistanceX(g-4,g9) = 3.85146
    c: Coincident(g10,g9)
    c: PointOnObject(g11,g-1)
    c: Parallel(g10,g11)
    c: Tangent(g-5,g11)
    c: Angle(g9,g10) = 2.35619
    c: PointOnObject(g11,g-2)
    c: Tangent(g10,g8)
    c: PointOnObject(g12,g10)
    c: PointOnObject(g12,g11)
    c: Perpendicular(g10,g12)
    c: Distance(g12) = 3.5
    c: PointOnObject(g10,g-1)
    c: PointOnObject(g13,g8)
    c: Coincident(g13,g12)
    c: PointOnObject(g14,g-5)
    c: Coincident(g12,g14)
    c: Tangent(g9,g8) = -1.5708
    c: PointOnObject(g15,g-1)
    c: Parallel(g15,g10)
    c: PointOnObject(g16,g8)
    c: PointOnObject(g16,g-1)
    c: Tangent(g16,g8)
    c: Parallel(g15,g16)
    c: Distance(g16,g15) = 3.45025
    c: Tangent(g15,g-6) = -1.5708
FEATURE [PartDesign::Pocket] Pocket
  BaseFeature = -> Fillet
  Direction = (0,0,1)
  Length = 10
  Length2 = 5
  Profile = -> Sketch
  ReferenceAxis = -> Sketch [N_Axis]
  Type = 0
FEATURE [PartDesign::CoordinateSystem] LCS_2
  AttacherType = Attacher::AttachEngine3D
  AttachmentOffset = pos=(0,0,0) rot=(1,0,0;3.14159rad)
  MapMode = 5
  Support = -> [Pocket]
FEATURE [Sketcher::SketchObject] Sketch008
  ExternalGeometry = -> [Pad001]
  FullyConstrained = true
  MapMode = 5
  Placement = pos=(0,0,16) rot=(1,0,0;3.14159rad)
  Support = -> [Pad001]
  sketch-geometry (11):
    g0: LineSegment StartX=8 StartY=-42.5 StartZ=0 EndX=28 EndY=-42.5 EndZ=0
    g1: LineSegment StartX=28 StartY=-42.5 StartZ=0 EndX=28 EndY=-67 EndZ=0
    g2: LineSegment StartX=28 StartY=-67 StartZ=0 EndX=8 EndY=-67 EndZ=0
    g3: LineSegment StartX=8 StartY=-67 StartZ=0 EndX=8 EndY=-42.5 EndZ=0
    g4: GeomPoint X=8 Y=-42.5 Z=0
    g5: GeomPoint X=4 Y=-42.5 Z=0
    g6: LineSegment StartX=4 StartY=-42.5 StartZ=0 EndX=8 EndY=-42.5 EndZ=0
    g7: LineSegment StartX=6 StartY=-17.8322 StartZ=0 EndX=36.5 EndY=-17.8322 EndZ=0
    g8: LineSegment StartX=36.5 StartY=-17.8322 StartZ=0 EndX=36.5 EndY=-29.3322 EndZ=0
    g9: LineSegment StartX=36.5 StartY=-29.3322 StartZ=0 EndX=6 EndY=-29.3322 EndZ=0
    g10: LineSegment StartX=6 StartY=-29.3322 StartZ=0 EndX=6 EndY=-17.8322 EndZ=0
  constraints (28):
    c: Coincident(g0,g1)
    c: Coincident(g1,g2)
    c: Coincident(g2,g3)
    c: Coincident(g3,g0)
    c: Horizontal(g0)
    c: Horizontal(g2)
    c: Vertical(g1)
    c: Vertical(g3)
    c: DistanceX(g0,g0) = 20
    c: Symmetric(g-3,g-3,g5)
    c: Coincident(g6,g5)
    c: Coincident(g6,g4)
    c: Horizontal(g6)
    c: DistanceX(g6,g6) = 4
    c: DistanceY(g3,g3) = 24.5
    c: Coincident(g0,g4)
    c: Coincident(g7,g8)
    c: Coincident(g8,g9)
    c: Coincident(g9,g10)
    c: Coincident(g10,g7)
    c: Horizontal(g7)
    c: Horizontal(g9)
    c: Vertical(g8)
    c: Vertical(g10)
    c: DistanceY(g8,g8) = 11.5
    c: DistanceX(g7,g7) = 30.5
    c: DistanceX(g-3,g7) = 2
    c: DistanceY(g7,g-3) = 2
FEATURE [PartDesign::Pocket] Pocket006
  BaseFeature = -> Pocket
  Direction = (0,0,1)
  Length = 2
  Length2 = 5
  Profile = -> Sketch008
  ReferenceAxis = -> Sketch008 [N_Axis]
  Refine = true
  Type = 0
FEATURE [PartDesign::Body] Body002  label="Front"
  Group = -> [Box002,Sketch001,Pocket001,Sketch002,Pocket002,Sketch003,Pocket003,Sketch004,Pad,Sketch005,Pocket004,Sketch007,Pad001,Sketch008,Fillet,Sketch,Pocket,LCS_2,Pocket006]
  Origin = -> Origin002
  Tip = -> Pocket006
COMPONENT P5 — geometry summary ("Tela OLed 128x64 v15"; no construction recipe available for this part):
  bounding box: 28.3 x 27.6 x 10.4 mm
  tessellated surface: 4,433 triangles
  volume: 2103 mm^3 (26% of its bounding box)
  symmetry: mirror-symmetric across its x mid-plane
PROVENANCE & LICENSES
A FreeCAD (.FCStd) document from a public repository crawl; recipes are the document's own serialized feature recipes (and, for linked parts, companion documents' recipes).
License: as declared in the source repository (recorded in the dataset sidecar).
